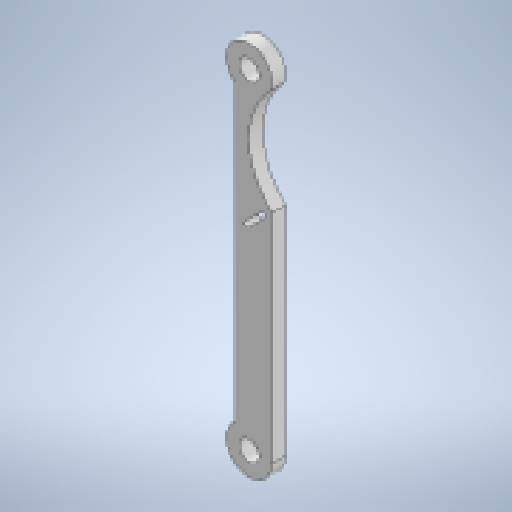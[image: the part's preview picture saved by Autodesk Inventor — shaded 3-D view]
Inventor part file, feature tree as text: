
AUTODESK INVENTOR PART (.ipt)
format: ipt  version: 2024 (Build 280153000, 153)  size: 196,608 bytes
history: native  units: mm
features: other x5, extrude x3, sketch x2, reference x2
ambient origin geometry x8: Origin, YZ Plane, XZ Plane, XY Plane, X Axis, Y Axis, Z Axis, Center Point
bodies: Body1 (feature_tree)
feature tree (12):
  other  "ソリッド1"
  extrude  "押し出し1"  Depth=2.2mm
  sketch  "スケッチ2"
  extrude  "押し出し2"  Depth=2.2mm
  extrude  "押し出し3"  Depth=5.0mm
  sketch  "スケッチ1"
  reference  "参照1"
  reference  "参照2"
  other  "<userpath>\OneDrive\ドキュメント\Inventor\Vixen\leg.iam"
  other  "leg.iam"
  other  "KRS2500_scale:2"
  other  "02157_SmallDiameterHornB:1"
